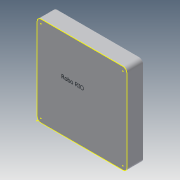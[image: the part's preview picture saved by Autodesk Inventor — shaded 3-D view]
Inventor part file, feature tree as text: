
AUTODESK INVENTOR PART (.ipt)
format: ipt  version: 2014 (Build 180170000, 170)  size: 86,016 bytes
history: native  units: in
note: dims shown in document units (in); Inventor stores cm internally (conversion verified against a paired STEP export)
features: sketch x2, extrude x1
ambient origin geometry x8: Origin, YZ Plane, XZ Plane, XY Plane, X Axis, Y Axis, Z Axis, Center Point
bodies: Solid1 (feature_tree)
feature tree (3):
  extrude  "Extrusion1"  Depth=5.625in
  sketch  "Sketch2"  dims[d2=0.25in d3=1.0in d4=0.0in]
  sketch  "Sketch1"  dims[d0=5.625in d1=5.625in]
